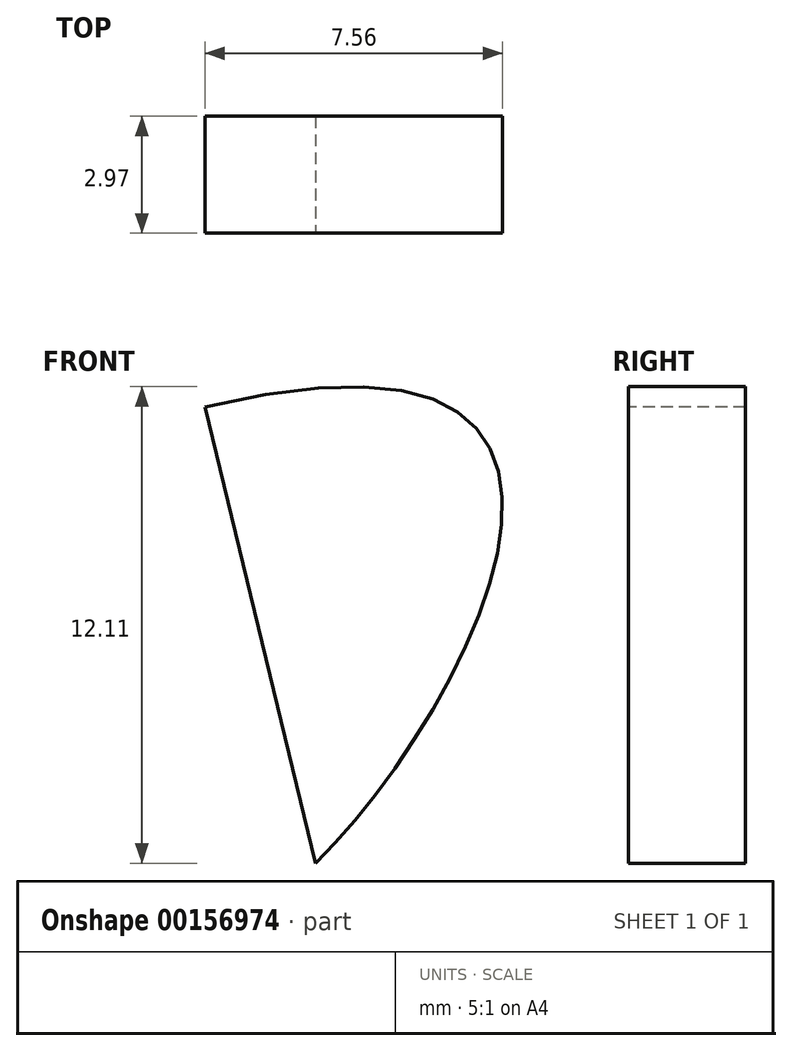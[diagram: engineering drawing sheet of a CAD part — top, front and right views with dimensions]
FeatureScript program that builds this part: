
annotation { "Feature Type Name" : "Feature", "Feature Type Description" : "" }
export const myFeature = defineFeature(function(context is Context, id is Id, definition is map)
    precondition{}
    {
        {
            var Q0;
            Q0=qCreatedBy(makeId("Front.planeOp"),FACE);
            var sketch = newSketch(context, id + "F0", { "sketchPlane" : qUnion([Q0])});
            skLineSegment(sketch, "E0", {"start": v(-82.98, -38.16) * mm, "end": v(120.22, -38.16) * mm});
            skLineSegment(sketch, "E1", {"start": v(120.22, -38.16) * mm, "end": v(227.98, 69.6) * mm});
            skFitSpline(sketch, "E2", {"points": [v(-82.98, -38.16) * mm, v(-45.71, -11.98) * mm, v(114.1, 0) * mm, v(227.98, 69.6) * mm], "startDerivative": vector(144.35, 97.65) * mm, "endDerivative": vector(194.09, -42.76) * mm});
            skArc(sketch, "E3", {"start": v(44.37, -38.16) * mm, "mid": v(10.29, 85.07) * mm, "end": v(-23.8, -38.16) * mm});
            skFitSpline(sketch, "E4", {"points": [v(114.1, 0) * mm, v(68.37, 50.77) * mm], "startDerivative": vector(-45.44, 0) * mm, "endDerivative": vector(-53.86, 89.45) * mm});
            skCircle(sketch, "E5", {"center": v(220.87, 69.6) * mm, "radius": 8.73 * mm});
            skSolve(sketch);
        }
        {
            var Q0;
            Q0 = qSketchRegion(id + "F0", true);
            var Q1;
            {var subQ0=sQuery(id+"F0.wireOp",EDGE,"E3");var subQ1=sQuery(id+"F0.wireOp",EDGE,"E2");var subQ2=makeQuery(id+"F0.imprint","INTERSECT",VERTEX,{"disambiguationData":[OD(0.0)],"derivedFrom":[subQ1,subQ0]});Q1=makeQuery(id+"F0.imprint","IMPRINT",FACE,{"disambiguationData":[TD([[makeQuery(id+"F0.imprint","IMPRINT",EDGE,{"disambiguationData":[TD([[subQ2,-1.0]])],"derivedFrom":subQ1}),-1.0]])]});}
            extrude(context, id + "F1", {"entities" : qUnion([Q0, Q1]), "depth" : 2.97 * mm});
        }
        {
            var Q0;
            Q0=makeQuery(id+"F1.opExtrude","CAP_FACE",FACE,{"disambiguationData":[OSD([sQuery(id+"F0.wireOp",EDGE,"E0"),sQuery(id+"F0.wireOp",EDGE,"E1"),sQuery(id+"F0.wireOp",EDGE,"E2"),sQuery(id+"F0.wireOp",EDGE,"E3"),sQuery(id+"F0.wireOp",EDGE,"E4"),sQuery(id+"F0.wireOp",EDGE,"E5")])],"isStart":false});
            var sketch = newSketch(context, id + "F2", { "sketchPlane" : qUnion([Q0])});
            skFitSpline(sketch, "E6", {"points": [v(6.23, 28.95) * mm, v(10.29, 18.75) * mm, v(0, 15.91) * mm, v(-10.05, 27.04) * mm, v(0, 41.62) * mm, v(11.05, 42.98) * mm, v(28.58, 32.92) * mm, v(32, 13.78) * mm, v(14.31, 0) * mm, v(-13.59, 0) * mm, v(-30.9, 14.12) * mm, v(-30.94, 35.55) * mm, v(-21.22, 53.04) * mm, v(0, 67.41) * mm, v(23.65, 66.7) * mm, v(50.2, 47.58) * mm, v(60.92, 19.67) * mm, v(22.82, -16.16) * mm, v(0, -21.12) * mm, v(-25.53, -20.22) * mm, v(-48.1, -12.73) * mm], "startDerivative": vector(958.72, 231.67) * mm, "endDerivative": vector(-435.44, 242.15) * mm});
            skFitSpline(sketch, "E7.0", {"points": [v(5.63, 31.41) * mm, v(6.31, 31.58) * mm, v(7.6, 31.84) * mm, v(9.34, 32.03) * mm, v(10.92, 32) * mm, v(12.38, 31.76) * mm, v(13.74, 31.2) * mm, v(14.93, 30.3) * mm, v(15.78, 29.12) * mm, v(16.23, 27.83) * mm, v(16.36, 26.57) * mm, v(16.28, 25.37) * mm, v(16.05, 24.23) * mm, v(15.59, 22.74) * mm, v(14.8, 20.96) * mm, v(13.61, 18.96) * mm, v(12.32, 17.17) * mm, v(11, 15.67) * mm, v(9.63, 14.44) * mm, v(8.16, 13.48) * mm, v(6.6, 12.81) * mm, v(5, 12.46) * mm, v(3.4, 12.42) * mm, v(1.86, 12.62) * mm, v(0.63, 12.96) * mm, v(-0.34, 13.3) * mm, v(-1.3, 13.69) * mm, v(-2.5, 14.25) * mm, v(-3.96, 15.06) * mm, v(-5.4, 15.98) * mm, v(-7.25, 17.38) * mm, v(-8.97, 19.02) * mm, v(-10.43, 20.9) * mm, v(-11.37, 22.44) * mm, v(-12.09, 24.11) * mm, v(-12.46, 25.61) * mm, v(-12.6, 26.88) * mm, v(-12.6, 28.15) * mm, v(-12.41, 29.7) * mm, v(-11.9, 31.5) * mm, v(-11.18, 33.23) * mm, v(-10.28, 34.88) * mm, v(-8.88, 36.99) * mm, v(-6.83, 39.4) * mm, v(-4.1, 41.91) * mm, v(-1.29, 43.9) * mm, v(1.5, 45.29) * mm, v(4.34, 46.04) * mm, v(7.2, 46.18) * mm, v(9.56, 45.9) * mm, v(11.5, 45.5) * mm, v(13, 45.12) * mm, v(14.55, 44.66) * mm, v(16.7, 43.94) * mm, v(19.44, 42.82) * mm, v(22.74, 41.13) * mm, v(25.4, 39.4) * mm, v(27.4, 37.8) * mm, v(28.82, 36.48) * mm, v(30.15, 35.06) * mm, v(31.76, 33) * mm, v(33.41, 30.2) * mm, v(34.82, 26.6) * mm, v(35.62, 22.86) * mm, v(35.78, 19.05) * mm, v(35.35, 15.92) * mm, v(34.64, 13.5) * mm, v(33.67, 11.15) * mm, v(32.03, 8.45) * mm, v(29.5, 5.6) * mm, v(26.51, 3.1) * mm, v(23.16, 0.96) * mm, v(19.52, -0.84) * mm, v(15.66, -2.3) * mm, v(10.33, -3.79) * mm, v(3.4, -4.8) * mm, v(-4.98, -4.64) * mm, v(-13.12, -3.08) * mm, v(-19.42, -0.55) * mm, v(-23.94, 2.17) * mm, v(-27.02, 4.56) * mm, v(-29.7, 7.3) * mm, v(-31.57, 9.86) * mm, v(-32.8, 12.07) * mm, v(-33.57, 13.81) * mm, v(-34.18, 15.6) * mm, v(-34.8, 18.04) * mm, v(-35.25, 21.15) * mm, v(-35.32, 24.93) * mm, v(-35.01, 28.68) * mm, v(-34.39, 32.36) * mm, v(-33.52, 35.9) * mm, v(-32.46, 39.26) * mm, v(-31.19, 42.48) * mm, v(-29.69, 45.56) * mm, v(-27.94, 48.53) * mm, v(-25.94, 51.4) * mm, v(-23.66, 54.18) * mm, v(-21.1, 56.9) * mm, v(-18.26, 59.54) * mm, v(-14.18, 62.88) * mm, v(-9.69, 65.86) * mm, v(-4.92, 68.27) * mm, v(-1.85, 69.5) * mm, v(0.65, 70.28) * mm, v(3.17, 70.93) * mm, v(7.6, 71.7) * mm, v(14, 71.78) * mm, v(20.41, 70.53) * mm, v(25.5, 68.77) * mm, v(30.54, 66.52) * mm, v(35.47, 63.61) * mm, v(40.24, 60.18) * mm, v(43.72, 57.36) * mm, v(47.1, 54.34) * mm, v(49.82, 51.68) * mm, v(51.92, 49.47) * mm, v(53.98, 47.22) * mm, v(56.45, 44.28) * mm, v(59.13, 40.58) * mm, v(61.4, 36.68) * mm, v(63.15, 32.56) * mm, v(64.2, 28.21) * mm, v(64.35, 24.42) * mm, v(63.96, 21.32) * mm, v(63.41, 18.97) * mm, v(62.58, 16.63) * mm, v(61.16, 13.54) * mm, v(58.85, 9.73) * mm, v(55.38, 5.28) * mm, v(51.35, 0.97) * mm, v(46.91, -3.15) * mm, v(40.62, -8.3) * mm, v(34.05, -12.85) * mm, v(27.75, -16.54) * mm, v(23.3, -18.81) * mm, v(19.2, -20.54) * mm, v(15.4, -21.8) * mm, v(11.81, -22.65) * mm, v(8.37, -23.18) * mm, v(5, -23.47) * mm, v(2.21, -23.6) * mm, v(-0.07, -23.66) * mm, v(-1.82, -23.7) * mm, v(-3.61, -23.74) * mm, v(-6.05, -23.77) * mm, v(-9.19, -23.78) * mm, v(-13.03, -23.72) * mm, v(-16.9, -23.57) * mm, v(-20.76, -23.32) * mm, v(-24.58, -22.93) * mm, v(-28.28, -22.4) * mm, v(-31.89, -21.7) * mm, v(-36.6, -20.51) * mm, v(-42.36, -18.51) * mm, v(-46.97, -16.27) * mm, v(-49.32, -14.97) * mm]});
            skLineSegment(sketch, "E8", {"start": v(6.23, 28.95) * mm, "end": v(9.72, 14.57) * mm});
            skLineSegment(sketch, "E9", {"start": v(-45.69, -14.01) * mm, "end": v(-46.83, -16.28) * mm});
            skSolve(sketch);
        }
        {
            var Q0;
            {var subQ0=sQuery(id+"F2.wireOp",EDGE,"E6");Q0=makeQuery(id+"F2.imprint","IMPRINT",FACE,{"disambiguationData":[TD([[makeQuery(id+"F2.imprint","IMPRINT",EDGE,{"derivedFrom":subQ0}),1.0]])]});}
            var Q1;
            Q1=sQuery(id+"F2.wireOp",EDGE,"19e04099-89d4-405e-b8b3-01408b52d3cf.0");
            var Q2;
            Q2=sQuery(id+"F2.wireOp",EDGE,"E6");
            var Q3;
            Q3=sQuery(id+"F2.wireOp",EDGE,"db0b1f68-838b-4a1e-b7c4-3fa9a650a84a");
            var Q4;
            Q4=sQuery(id+"F2.wireOp",EDGE,"ebea1f15-5b8e-4fc7-89e0-73956c52e1f4");
            var Q5;
            Q5=sQuery(id+"F2.wireOp",EDGE,"72aedc0c-90ed-4d8b-b6be-333537171716.trimOffspring");
            var Q6;
            Q6=sQuery(id+"F2.wireOp",EDGE,"1f9c92d8-be09-49ca-9889-a9edf046b17e");
            var Q7;
            Q7=sQuery(id+"F2.wireOp",EDGE,"ad84ad96-0895-4e0c-bf7a-de2ea783b2a2");
            extrude(context, id + "F3", {"entities" : qUnion([Q0]), "operationType" : NewBodyOperationType.REMOVE, "surfaceEntities" : qUnion([Q1, Q2, Q3, Q4, Q5, Q6, Q7]), "endBound" : BoundingType.THROUGH_ALL, "oppositeDirection" : true, "depth" : 25.4 * mm});
        }
        {
            var Q0;
            Q0=makeQuery(id+"F1.opExtrude","CAP_FACE",FACE,{"disambiguationData":[OSD([sQuery(id+"F0.wireOp",EDGE,"E0"),sQuery(id+"F0.wireOp",EDGE,"E1"),sQuery(id+"F0.wireOp",EDGE,"E2"),sQuery(id+"F0.wireOp",EDGE,"E3"),sQuery(id+"F0.wireOp",EDGE,"E4"),sQuery(id+"F0.wireOp",EDGE,"E5")])],"isStart":false});
            var sketch = newSketch(context, id + "F4", { "sketchPlane" : qUnion([Q0])});
            skFitSpline(sketch, "E10", {"points": [v(114.1, 0) * mm, v(92.42, -10.52) * mm, v(68.97, -14.01) * mm, v(44.87, -4.8) * mm], "startDerivative": vector(-63.97, -35.04) * mm, "endDerivative": vector(-69.88, 35.87) * mm});
            skLineSegment(sketch, "E11", {"start": v(49.98, -4.53) * mm, "end": v(47.98, -6.4) * mm});
            skFitSpline(sketch, "E12", {"points": [v(49.98, -4.53) * mm, v(53.53, -6.45) * mm, v(68.84, -11.51) * mm, v(91.02, -8.81) * mm, v(105.66, -2.84) * mm, v(110.54, 0.39) * mm], "startDerivative": vector(24.69, -14.22) * mm, "endDerivative": vector(29.67, 21.88) * mm});
            skLineSegment(sketch, "E13", {"start": v(107.05, -2.03) * mm, "end": v(110.38, -2.03) * mm});
            skSolve(sketch);
        }
        {
            var Q0;
            Q0=makeQuery(id+"F4.imprint","IMPRINT",FACE,{"disambiguationData":[TD([[makeQuery(id+"F4.imprint","IMPRINT",EDGE,{"derivedFrom":sQuery(id+"F4.wireOp",EDGE,"E10")}),-1.0]])]});
            extrude(context, id + "F5", {"entities" : qUnion([Q0]), "operationType" : NewBodyOperationType.REMOVE, "oppositeDirection" : true, "depth" : 25.4 * mm});
        }
        {
            var Q0;
            Q0=makeQuery(id+"F1.opExtrude","CAP_FACE",FACE,{"disambiguationData":[OSD([sQuery(id+"F0.wireOp",EDGE,"E0"),sQuery(id+"F0.wireOp",EDGE,"E1"),sQuery(id+"F0.wireOp",EDGE,"E2"),sQuery(id+"F0.wireOp",EDGE,"E3"),sQuery(id+"F0.wireOp",EDGE,"E4"),sQuery(id+"F0.wireOp",EDGE,"E5")])],"isStart":false});
            var sketch = newSketch(context, id + "F6", { "sketchPlane" : qUnion([Q0])});
            skLineSegment(sketch, "E14.bottom", {"start": v(97.36, -35.62) * mm, "end": v(107.52, -35.62) * mm});
            skLineSegment(sketch, "E14.top", {"start": v(97.36, -32.64) * mm, "end": v(107.52, -32.64) * mm});
            skLineSegment(sketch, "E14.left", {"start": v(97.36, -35.62) * mm, "end": v(97.36, -32.64) * mm});
            skLineSegment(sketch, "E14.right", {"start": v(107.52, -35.62) * mm, "end": v(107.52, -32.64) * mm});
            skLineSegment(sketch, "E15.1.0.0", {"start": v(21.16, -32.64) * mm, "end": v(31.32, -32.64) * mm});
            skLineSegment(sketch, "E15.1.0.1", {"start": v(31.32, -35.62) * mm, "end": v(31.32, -32.64) * mm});
            skLineSegment(sketch, "E15.1.0.2", {"start": v(21.16, -35.62) * mm, "end": v(31.32, -35.62) * mm});
            skLineSegment(sketch, "E15.1.0.3", {"start": v(21.16, -35.62) * mm, "end": v(21.16, -32.64) * mm});
            skLineSegment(sketch, "E15.2.0.0", {"start": v(-55.04, -32.64) * mm, "end": v(-44.88, -32.64) * mm});
            skLineSegment(sketch, "E15.2.0.1", {"start": v(-44.88, -35.62) * mm, "end": v(-44.88, -32.64) * mm});
            skLineSegment(sketch, "E15.2.0.2", {"start": v(-55.04, -35.62) * mm, "end": v(-44.88, -35.62) * mm});
            skLineSegment(sketch, "E15.2.0.3", {"start": v(-55.04, -35.62) * mm, "end": v(-55.04, -32.64) * mm});
            skLineSegment(sketch, "E15.direction1", {"start": v(97.36, -32.64) * mm, "end": v(21.16, -32.64) * mm, "construction": true});
            skLineSegment(sketch, "E16", {"start": v(123.8, -30.97) * mm, "end": v(131, -23.79) * mm});
            skLineSegment(sketch, "E17", {"start": v(131, -23.79) * mm, "end": v(128.9, -21.69) * mm});
            skLineSegment(sketch, "E18", {"start": v(128.9, -21.69) * mm, "end": v(121.7, -28.87) * mm});
            skLineSegment(sketch, "E19", {"start": v(121.7, -28.87) * mm, "end": v(123.8, -30.97) * mm});
            skLineSegment(sketch, "E20", {"start": v(120.22, -38.16) * mm, "end": v(106.51, -24.45) * mm, "construction": true});
            skLineSegment(sketch, "E21", {"start": v(128.9, -21.69) * mm, "end": v(164, 13.42) * mm, "construction": true});
            skLineSegment(sketch, "E22.1.0.0", {"start": v(169.28, 18.74) * mm, "end": v(162.1, 11.56) * mm});
            skLineSegment(sketch, "E22.1.0.1", {"start": v(162.1, 11.56) * mm, "end": v(164.2, 9.46) * mm});
            skLineSegment(sketch, "E22.1.0.2", {"start": v(164.2, 9.46) * mm, "end": v(171.39, 16.64) * mm});
            skLineSegment(sketch, "E22.1.0.3", {"start": v(171.39, 16.64) * mm, "end": v(169.28, 18.74) * mm});
            skLineSegment(sketch, "E22.2.0.0", {"start": v(209.68, 59.17) * mm, "end": v(202.5, 51.99) * mm});
            skLineSegment(sketch, "E22.2.0.1", {"start": v(202.5, 51.99) * mm, "end": v(204.6, 49.88) * mm});
            skLineSegment(sketch, "E22.2.0.2", {"start": v(204.6, 49.88) * mm, "end": v(211.78, 57.07) * mm});
            skLineSegment(sketch, "E22.2.0.3", {"start": v(211.78, 57.07) * mm, "end": v(209.68, 59.17) * mm});
            skLineSegment(sketch, "E22.direction1", {"start": v(121.7, -28.87) * mm, "end": v(162.1, 11.56) * mm, "construction": true});
            skSolve(sketch);
        }
        {
            var Q0;
            Q0 = qSketchRegion(id + "F6", true);
            extrude(context, id + "F7", {"entities" : qUnion([Q0]), "operationType" : NewBodyOperationType.REMOVE, "endBound" : BoundingType.THROUGH_ALL, "oppositeDirection" : true, "depth" : 25.4 * mm});
        }
    });
